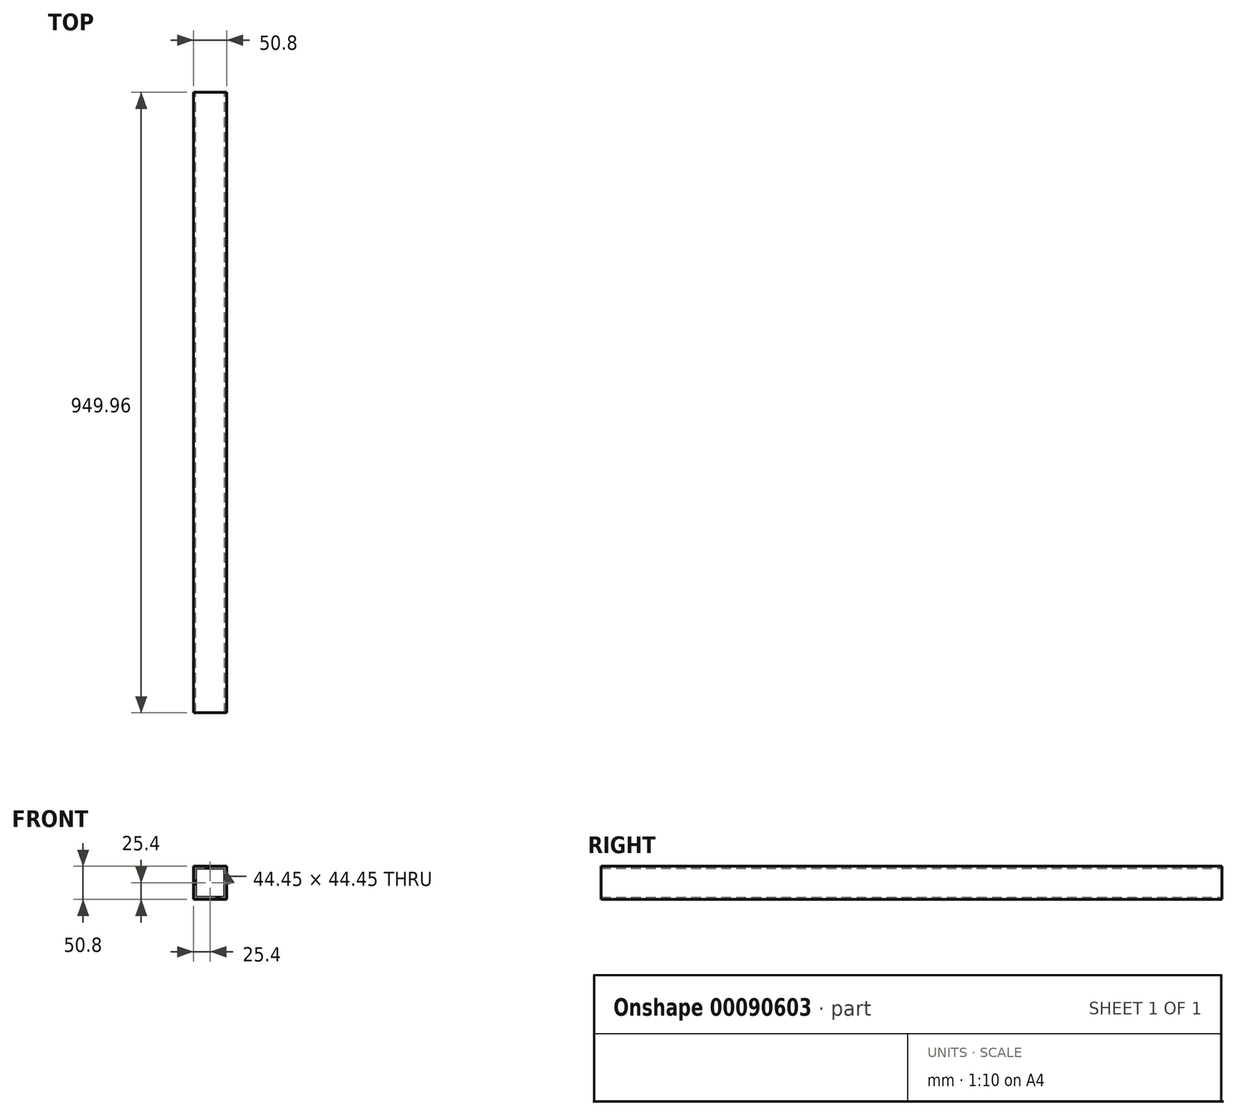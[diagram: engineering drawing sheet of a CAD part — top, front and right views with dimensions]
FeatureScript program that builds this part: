
annotation { "Feature Type Name" : "Feature", "Feature Type Description" : "" }
export const myFeature = defineFeature(function(context is Context, id is Id, definition is map)
    precondition{}
    {
        {
            var Q0;
            Q0=qCreatedBy(makeId("Front.planeOp"),FACE);
            var sketch = newSketch(context, id + "F0", { "sketchPlane" : qUnion([Q0])});
            skLineSegment(sketch, "E0.bottom", {"start": v(25.4, 25.4) * mm, "end": v(-25.4, 25.4) * mm});
            skLineSegment(sketch, "E0.top", {"start": v(25.4, -25.4) * mm, "end": v(-25.4, -25.4) * mm});
            skLineSegment(sketch, "E0.left", {"start": v(25.4, 25.4) * mm, "end": v(25.4, -25.4) * mm});
            skLineSegment(sketch, "E0.right", {"start": v(-25.4, 25.4) * mm, "end": v(-25.4, -25.4) * mm});
            skPoint(sketch, "E0.middle", {"position": v(0, 0) * mm});
            skLineSegment(sketch, "E1.bottom", {"start": v(22.23, 22.23) * mm, "end": v(-22.23, 22.23) * mm});
            skLineSegment(sketch, "E1.top", {"start": v(22.23, -22.23) * mm, "end": v(-22.23, -22.23) * mm});
            skLineSegment(sketch, "E1.left", {"start": v(22.23, 22.23) * mm, "end": v(22.23, -22.23) * mm});
            skLineSegment(sketch, "E1.right", {"start": v(-22.23, 22.23) * mm, "end": v(-22.23, -22.23) * mm});
            skSolve(sketch);
        }
        {
            var Q0;
            Q0 = qSketchRegion(id + "F0", true);
            extrude(context, id + "F1", {"entities" : qUnion([Q0]), "endBound" : BoundingType.SYMMETRIC, "depth" : 949.96 * mm});
        }
    });
